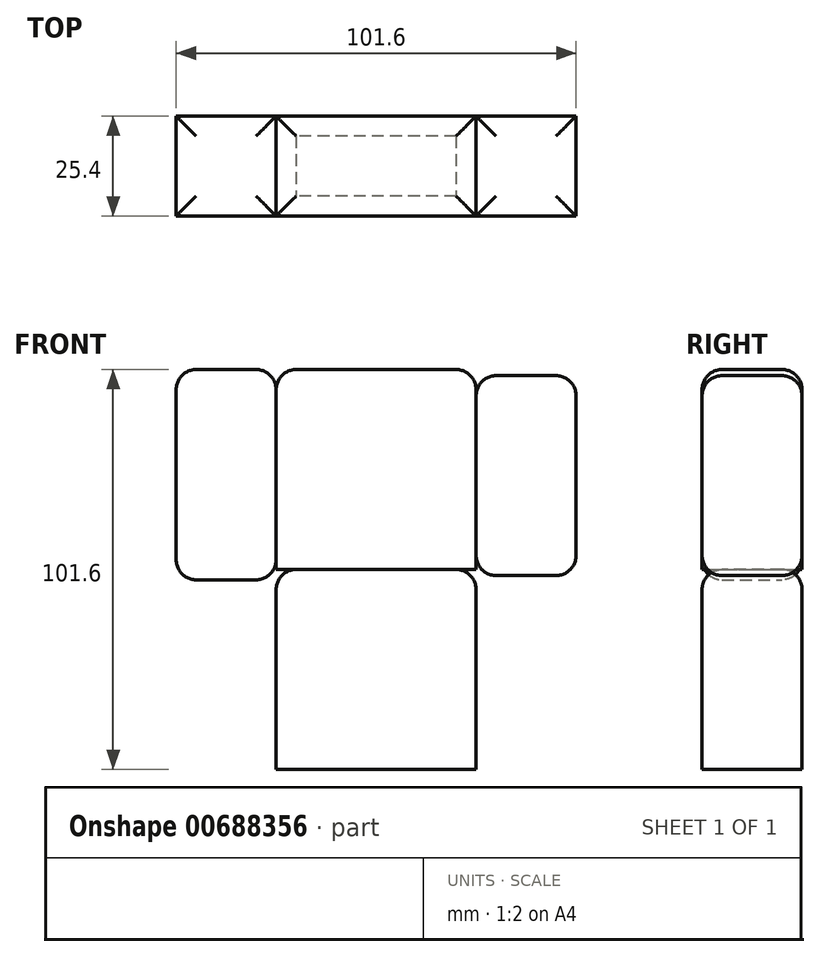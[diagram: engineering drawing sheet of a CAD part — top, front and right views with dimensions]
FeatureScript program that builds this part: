
annotation { "Feature Type Name" : "Feature", "Feature Type Description" : "" }
export const myFeature = defineFeature(function(context is Context, id is Id, definition is map)
    precondition{}
    {
        {
            var Q0;
            Q0=qCreatedBy(makeId("Top.planeOp"),FACE);
            var sketch = newSketch(context, id + "F0", { "sketchPlane" : qUnion([Q0])});
            skLineSegment(sketch, "E0.bottom", {"start": v(12.7, 12.7) * mm, "end": v(-12.7, 12.7) * mm});
            skLineSegment(sketch, "E0.top", {"start": v(12.7, -12.7) * mm, "end": v(-12.7, -12.7) * mm});
            skLineSegment(sketch, "E0.left", {"start": v(12.7, 12.7) * mm, "end": v(12.7, -12.7) * mm});
            skLineSegment(sketch, "E0.right", {"start": v(-12.7, 12.7) * mm, "end": v(-12.7, -12.7) * mm});
            skPoint(sketch, "E0.middle", {"position": v(0, 0) * mm});
            skLineSegment(sketch, "E1.bottom", {"start": v(12.7, 12.7) * mm, "end": v(38.1, 12.7) * mm});
            skLineSegment(sketch, "E1.top", {"start": v(12.7, -12.7) * mm, "end": v(38.1, -12.7) * mm});
            skLineSegment(sketch, "E1.right", {"start": v(38.1, 12.7) * mm, "end": v(38.1, -12.7) * mm});
            skSolve(sketch);
        }
        {
            var Q0;
            Q0 = qSketchRegion(id + "F0", true);
            extrude(context, id + "F1", {"entities" : qUnion([Q0]), "depth" : 50.8 * mm, "offsetDistance" : 25.4 * mm});
        }
        {
            var Q0;
            Q0=makeQuery(id+"F1.opExtrude","CAP_FACE",FACE,{"disambiguationData":[OSD([sQuery(id+"F0.wireOp",EDGE,"E0.bottom"),sQuery(id+"F0.wireOp",EDGE,"E0.top"),sQuery(id+"F0.wireOp",EDGE,"E0.right"),sQuery(id+"F0.wireOp",EDGE,"E1.bottom"),sQuery(id+"F0.wireOp",EDGE,"E1.top"),sQuery(id+"F0.wireOp",EDGE,"E1.right")])],"isStart":false});
            fillet(context, id + "F2", {"entities" : qUnion([Q0]), "radius" : 5.08 * mm, "tangentPropagation" : true, "allowEdgeOverflow" : false});
        }
        {
            var Q0;
            Q0=makeQuery(id+"F1.opExtrude","CAP_FACE",FACE,{"disambiguationData":[OSD([sQuery(id+"F0.wireOp",EDGE,"E0.bottom"),sQuery(id+"F0.wireOp",EDGE,"E0.top"),sQuery(id+"F0.wireOp",EDGE,"E0.right"),sQuery(id+"F0.wireOp",EDGE,"E1.bottom"),sQuery(id+"F0.wireOp",EDGE,"E1.top"),sQuery(id+"F0.wireOp",EDGE,"E1.right")])],"isStart":false});
            var sketch = newSketch(context, id + "F3", { "sketchPlane" : qUnion([Q0])});
            skLineSegment(sketch, "E2.bottom", {"start": v(38.1, -12.7) * mm, "end": v(-12.7, -12.7) * mm});
            skLineSegment(sketch, "E2.top", {"start": v(38.1, 12.7) * mm, "end": v(-12.7, 12.7) * mm});
            skLineSegment(sketch, "E2.left", {"start": v(38.1, -12.7) * mm, "end": v(38.1, 12.7) * mm});
            skLineSegment(sketch, "E2.right", {"start": v(-12.7, -12.7) * mm, "end": v(-12.7, 12.7) * mm});
            skPoint(sketch, "E2.middle", {"position": v(12.7, 0) * mm});
            skPoint(sketch, "E2.middle.positionSnap0", {"position": v(12.7, 7.62) * mm});
            skPoint(sketch, "E2.centerSnap0", {"position": v(12.7, 7.62) * mm});
            skSolve(sketch);
        }
        {
            var Q0;
            Q0 = qSketchRegion(id + "F3", true);
            extrude(context, id + "F4", {"entities" : qUnion([Q0]), "operationType" : NewBodyOperationType.ADD, "depth" : 50.8 * mm, "offsetDistance" : 25.4 * mm});
        }
        {
            var Q0;
            Q0=makeQuery(id+"F4.opExtrude","SWEPT_FACE",FACE,{"disambiguationData":[OSD([sQuery(id+"F3.wireOp",EDGE,"E2.right")])]});
            var sketch = newSketch(context, id + "F5", { "sketchPlane" : qUnion([Q0])});
            skLineSegment(sketch, "E3.bottom", {"start": v(12.7, 101.6) * mm, "end": v(-12.7, 101.6) * mm});
            skLineSegment(sketch, "E3.top", {"start": v(12.7, 48.18) * mm, "end": v(-12.7, 48.18) * mm});
            skLineSegment(sketch, "E3.left", {"start": v(12.7, 101.6) * mm, "end": v(12.7, 48.18) * mm});
            skLineSegment(sketch, "E3.right", {"start": v(-12.7, 101.6) * mm, "end": v(-12.7, 48.18) * mm});
            skPoint(sketch, "E3.middle", {"position": v(0, 74.89) * mm});
            skSolve(sketch);
        }
        {
            var Q0;
            Q0 = qSketchRegion(id + "F5", true);
            extrude(context, id + "F6", {"entities" : qUnion([Q0]), "depth" : 25.4 * mm, "offsetDistance" : 25.4 * mm});
        }
        {
            var Q0;
            Q0=makeQuery(id+"F4.opExtrude","SWEPT_FACE",FACE,{"disambiguationData":[OSD([sQuery(id+"F3.wireOp",EDGE,"E2.left")])]});
            var sketch = newSketch(context, id + "F7", { "sketchPlane" : qUnion([Q0])});
            skSolve(sketch);
        }
        {
            var Q0;
            {var subQ0=sQuery(id+"F3.wireOp",EDGE,"E2.left");Q0=makeQuery(id+"F7.imprint","IMPRINT",FACE,{"disambiguationData":[TD([[makeQuery(id+"F7.imprint","IMPRINT",EDGE,{"derivedFrom":makeQuery(id+"F4.opExtrude","CAP_EDGE",EDGE,{"disambiguationData":[OSD([subQ0])],"isStart":true})}),1.0]])]});}
            var sketch = newSketch(context, id + "F8", { "sketchPlane" : qUnion([Q0])});
            skLineSegment(sketch, "E4.bottom", {"start": v(12.7, 100.05) * mm, "end": v(-12.7, 100.05) * mm});
            skLineSegment(sketch, "E4.top", {"start": v(12.7, 49.25) * mm, "end": v(-12.7, 49.25) * mm});
            skLineSegment(sketch, "E4.left", {"start": v(12.7, 100.05) * mm, "end": v(12.7, 49.25) * mm});
            skLineSegment(sketch, "E4.right", {"start": v(-12.7, 100.05) * mm, "end": v(-12.7, 49.25) * mm});
            skPoint(sketch, "E4.middle", {"position": v(0, 74.65) * mm});
            skSolve(sketch);
        }
        {
            var Q0;
            Q0 = qSketchRegion(id + "F8", true);
            extrude(context, id + "F9", {"entities" : qUnion([Q0]), "depth" : 25.4 * mm, "offsetDistance" : 25.4 * mm});
        }
        {
            var Q0;
            Q0=makeQuery(id+"F6.opExtrude","SWEPT_FACE",FACE,{"disambiguationData":[OSD([sQuery(id+"F5.wireOp",EDGE,"E3.bottom")])]});
            var Q1;
            Q1=makeQuery(id+"F9.opExtrude","SWEPT_FACE",FACE,{"disambiguationData":[OSD([sQuery(id+"F8.wireOp",EDGE,"E4.bottom")])]});
            var Q2;
            Q2=makeQuery(id+"F4.opExtrude","CAP_FACE",FACE,{"disambiguationData":[OSD([sQuery(id+"F3.wireOp",EDGE,"E2.bottom"),sQuery(id+"F3.wireOp",EDGE,"E2.top"),sQuery(id+"F3.wireOp",EDGE,"E2.left"),sQuery(id+"F3.wireOp",EDGE,"E2.right")])],"isStart":false});
            var Q3;
            Q3=makeQuery(id+"F9.opExtrude","SWEPT_FACE",FACE,{"disambiguationData":[OSD([sQuery(id+"F8.wireOp",EDGE,"E4.top")])]});
            var Q4;
            Q4=makeQuery(id+"F6.opExtrude","SWEPT_FACE",FACE,{"disambiguationData":[OSD([sQuery(id+"F5.wireOp",EDGE,"E3.top")])]});
            fillet(context, id + "F10", {"entities" : qUnion([Q0, Q1, Q2, Q3, Q4]), "radius" : 5.08 * mm, "tangentPropagation" : true, "allowEdgeOverflow" : false});
        }
    });
